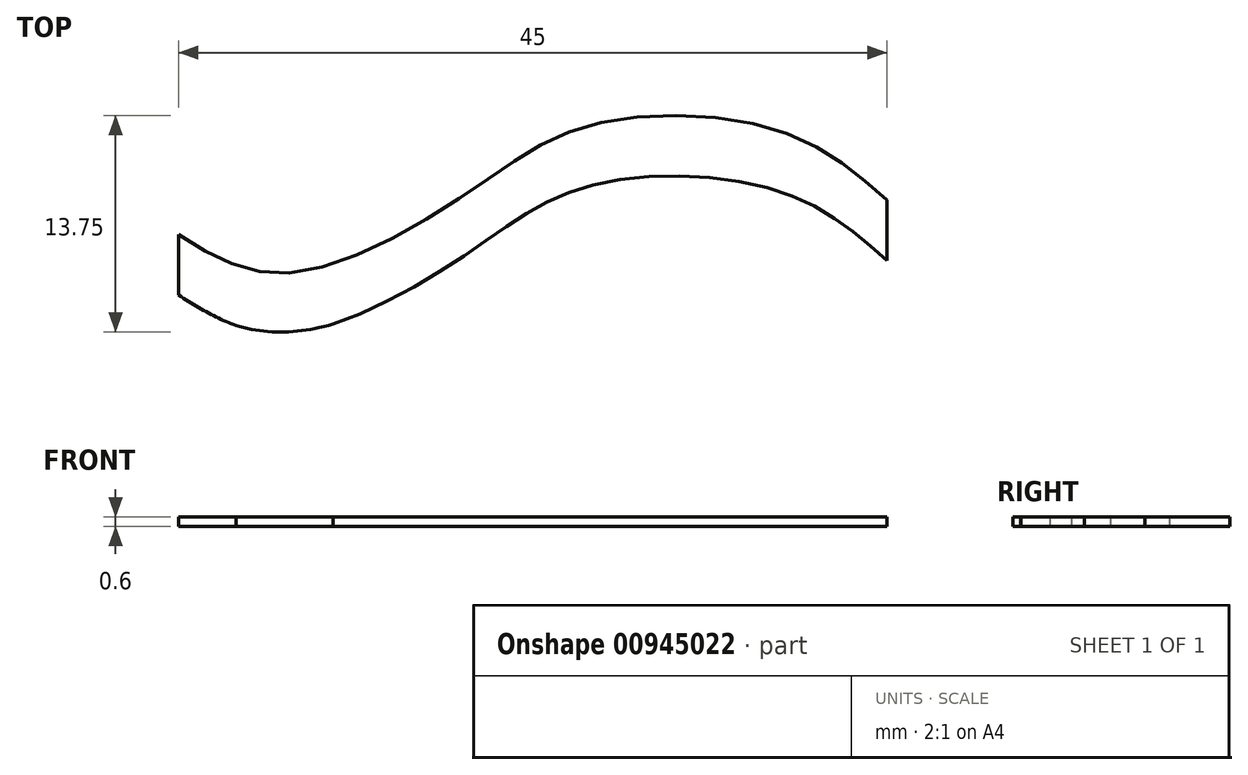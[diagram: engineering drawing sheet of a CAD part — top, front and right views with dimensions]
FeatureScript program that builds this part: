
annotation { "Feature Type Name" : "Feature", "Feature Type Description" : "" }
export const myFeature = defineFeature(function(context is Context, id is Id, definition is map)
    precondition{}
    {
        {
            var Q0;
            Q0=qCreatedBy(makeId("Top.planeOp"),FACE);
            var sketch = newSketch(context, id + "F0", { "sketchPlane" : qUnion([Q0])});
            skFitSpline(sketch, "E0", {"points": [v(-27.68, 4.36) * mm, v(-20.54, 1.95) * mm, v(-9.46, 6.91) * mm, v(-1.63, 11.29) * mm, v(10.58, 10.92) * mm, v(17.32, 6.55) * mm], "startDerivative": vector(39.5, -25.75) * mm, "endDerivative": vector(31.84, -28.11) * mm});
            skFitSpline(sketch, "E1", {"points": [v(-27.68, 0.32) * mm, v(-19.92, -1.74) * mm, v(-9.46, 2.87) * mm, v(-1.63, 7.25) * mm, v(10.58, 6.88) * mm, v(17.32, 2.5) * mm], "startDerivative": vector(39.5, -25.75) * mm, "endDerivative": vector(31.84, -28.11) * mm});
            skLineSegment(sketch, "E2", {"start": v(-27.68, 4.36) * mm, "end": v(-27.68, 0.32) * mm});
            skLineSegment(sketch, "E3", {"start": v(17.32, 6.55) * mm, "end": v(17.32, 2.5) * mm});
            skFitSpline(sketch, "E4", {"points": [v(-27.68, 0.53) * mm, v(-20.54, -1.89) * mm, v(-9.46, 3.08) * mm, v(-1.63, 7.45) * mm, v(10.58, 7.09) * mm, v(17.32, 2.71) * mm], "startDerivative": vector(39.5, -25.75) * mm, "endDerivative": vector(31.84, -28.11) * mm});
            skFitSpline(sketch, "E5", {"points": [v(-27.68, -3.51) * mm, v(-19.92, -5.58) * mm, v(-9.46, -0.96) * mm, v(-1.63, 3.41) * mm, v(10.58, 3.05) * mm, v(17.32, -1.32) * mm], "startDerivative": vector(39.5, -25.75) * mm, "endDerivative": vector(31.84, -28.11) * mm});
            skLineSegment(sketch, "E6", {"start": v(-27.68, 0.53) * mm, "end": v(-27.68, -3.51) * mm});
            skLineSegment(sketch, "E7", {"start": v(17.32, 2.71) * mm, "end": v(17.32, -1.32) * mm});
            skFitSpline(sketch, "E8", {"points": [v(-27.68, -3.2) * mm, v(-20.54, -5.6) * mm, v(-9.46, -0.64) * mm, v(-1.63, 3.73) * mm, v(10.58, 3.37) * mm, v(17.32, -1) * mm], "startDerivative": vector(39.5, -25.75) * mm, "endDerivative": vector(31.84, -28.11) * mm});
            skFitSpline(sketch, "E9", {"points": [v(-27.68, -7.23) * mm, v(-19.92, -9.3) * mm, v(-9.46, -4.68) * mm, v(-1.63, -0.3) * mm, v(10.58, -0.67) * mm, v(17.32, -5.04) * mm], "startDerivative": vector(39.5, -25.75) * mm, "endDerivative": vector(31.84, -28.11) * mm});
            skLineSegment(sketch, "E10", {"start": v(-27.68, -3.2) * mm, "end": v(-27.68, -7.23) * mm});
            skLineSegment(sketch, "E11", {"start": v(17.32, -1) * mm, "end": v(17.32, -5.04) * mm});
            skFitSpline(sketch, "E12", {"points": [v(-31.13, -12.74) * mm, v(-23.99, -15.15) * mm, v(-12.92, -10.19) * mm, v(-5.08, -5.81) * mm, v(7.12, -6.18) * mm, v(13.87, -10.55) * mm], "startDerivative": vector(39.5, -25.75) * mm, "endDerivative": vector(31.84, -28.11) * mm});
            skFitSpline(sketch, "E13", {"points": [v(-31.13, -16.78) * mm, v(-23.37, -18.84) * mm, v(-12.92, -14.23) * mm, v(-5.08, -9.85) * mm, v(7.12, -10.22) * mm, v(13.87, -14.59) * mm], "startDerivative": vector(39.5, -25.75) * mm, "endDerivative": vector(31.84, -28.11) * mm});
            skLineSegment(sketch, "E14", {"start": v(-31.13, -12.74) * mm, "end": v(-31.13, -16.78) * mm});
            skLineSegment(sketch, "E15", {"start": v(13.87, -10.55) * mm, "end": v(13.87, -14.59) * mm});
            skSolve(sketch);
        }
        {
            var Q0;
            Q0=makeQuery(id+"F0.imprint","IMPRINT",FACE,{"disambiguationData":[TD([[makeQuery(id+"F0.imprint","IMPRINT",EDGE,{"derivedFrom":sQuery(id+"F0.wireOp",EDGE,"E0")}),-1.0]])]});
            extrude(context, id + "F1", {"entities" : qUnion([Q0]), "depth" : 0.6 * mm, "offsetDistance" : 25 * mm});
        }
    });
